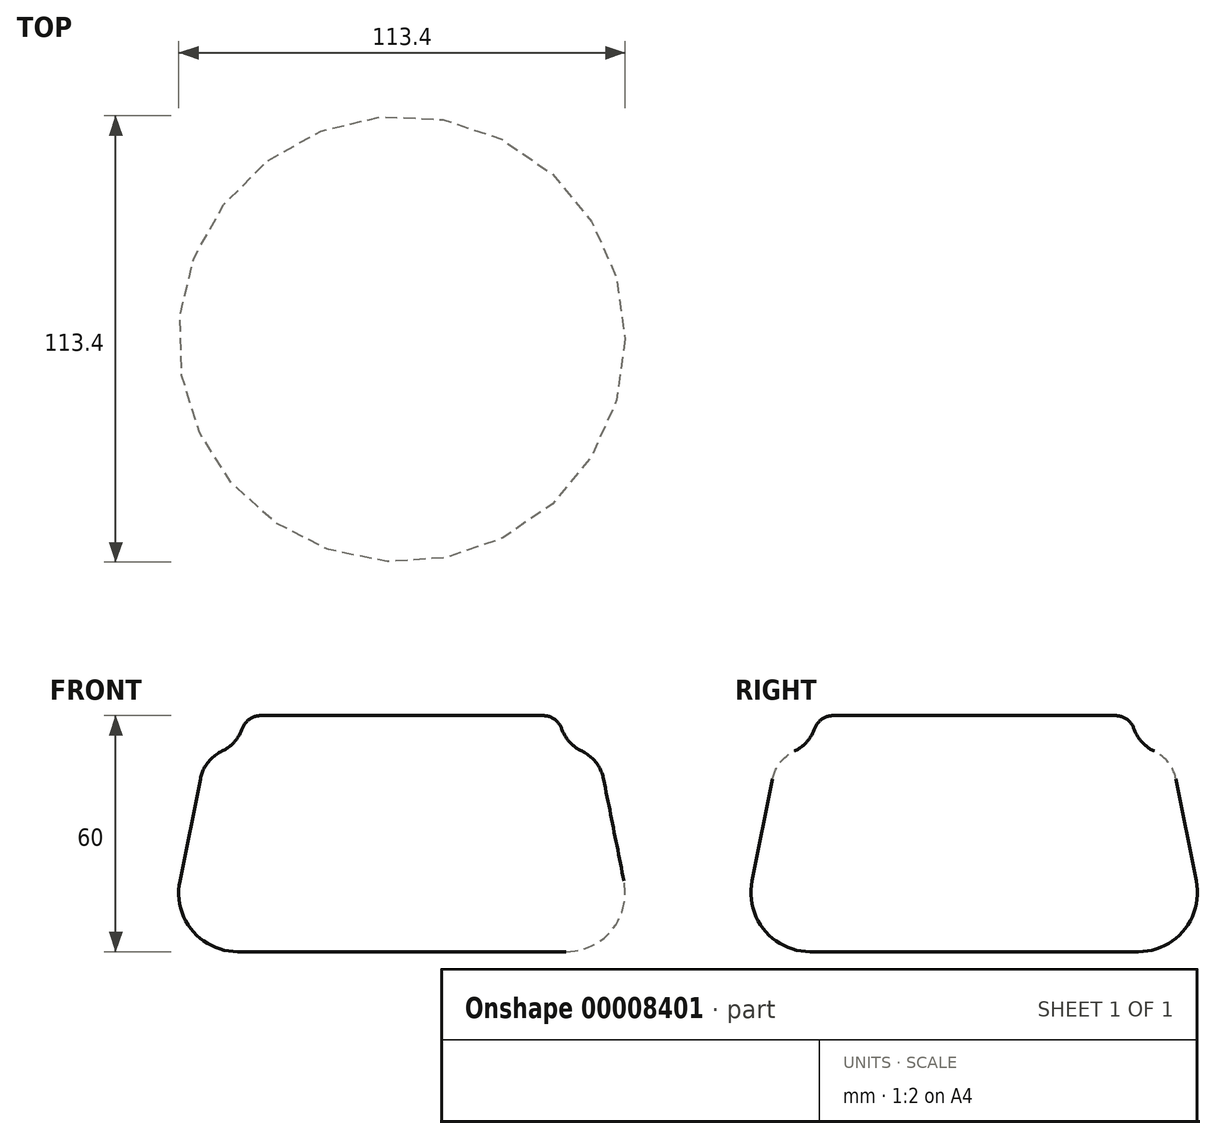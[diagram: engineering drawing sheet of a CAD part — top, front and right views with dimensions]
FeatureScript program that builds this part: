
annotation { "Feature Type Name" : "Feature", "Feature Type Description" : "" }
export const myFeature = defineFeature(function(context is Context, id is Id, definition is map)
    precondition{}
    {
        {
            var Q0;
            Q0=qCreatedBy(makeId("Right.planeOp"),FACE);
            var sketch = newSketch(context, id + "F0", { "sketchPlane" : qUnion([Q0])});
            skLineSegment(sketch, "E0", {"start": v(0, 0) * mm, "end": v(-41.7, 0) * mm});
            skLineSegment(sketch, "E1", {"start": v(-56.41, 17.94) * mm, "end": v(-51.22, 43.9) * mm});
            skLineSegment(sketch, "E2", {"start": v(-35.86, 60) * mm, "end": v(0, 60) * mm});
            skArc(sketch, "E3", {"start": v(-45.7, 50.97) * mm, "mid": v(-42.57, 53.3) * mm, "end": v(-40.57, 56.67) * mm});
            skLineSegment(sketch, "E4", {"start": v(-40, 60) * mm, "end": v(-40, 50) * mm, "construction": true});
            skLineSegment(sketch, "E5", {"start": v(-40, 50) * mm, "end": v(-50, 50) * mm, "construction": true});
            skPoint(sketch, "E6.visualSharp", {"position": v(-60, 0) * mm});
            skArc(sketch, "E6.filletArc", {"start": v(-56.41, 17.94) * mm, "mid": v(-53.3, 5.5) * mm, "end": v(-41.7, 0) * mm});
            skPoint(sketch, "E7.visualSharp", {"position": v(-50, 50) * mm});
            skArc(sketch, "E7.filletArc", {"start": v(-45.7, 50.97) * mm, "mid": v(-49.3, 48.09) * mm, "end": v(-51.22, 43.9) * mm});
            skPoint(sketch, "E8.visualSharp", {"position": v(-40, 60) * mm});
            skArc(sketch, "E8.filletArc", {"start": v(-35.86, 60) * mm, "mid": v(-38.74, 59.08) * mm, "end": v(-40.57, 56.67) * mm});
            skLineSegment(sketch, "E9", {"start": v(0, 60) * mm, "end": v(0, 0) * mm});
            skSolve(sketch);
        }
        {
            var Q0;
            Q0=makeQuery(id+"F0.imprint","IMPRINT",FACE,{"disambiguationData":[TD([[makeQuery(id+"F0.imprint","IMPRINT",EDGE,{"derivedFrom":sQuery(id+"F0.wireOp",EDGE,"E0")}),-1.0]])]});
            var Q1;
            Q1=sQuery(id+"F0.wireOp",EDGE,"E9");
            revolve(context, id + "F1", {"entities" : qUnion([Q0]), "axis" : qUnion([Q1]), "revolveType" : RevolveType.FULL});
        }
    });
